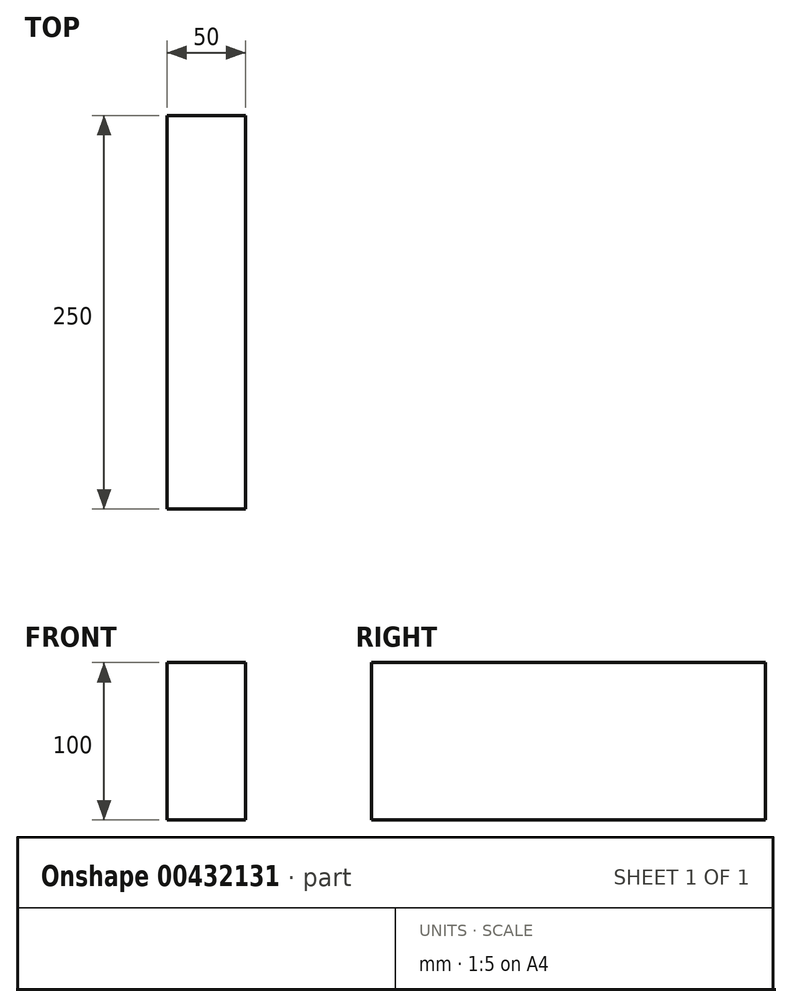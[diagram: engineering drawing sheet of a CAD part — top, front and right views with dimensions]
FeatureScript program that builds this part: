
annotation { "Feature Type Name" : "Feature", "Feature Type Description" : "" }
export const myFeature = defineFeature(function(context is Context, id is Id, definition is map)
    precondition{}
    {
        {
            var Q0;
            Q0=qCreatedBy(makeId("Right.planeOp"),FACE);
            var sketch = newSketch(context, id + "F0", { "sketchPlane" : qUnion([Q0])});
            skLineSegment(sketch, "E0.bottom", {"start": v(54.73, -201.24) * mm, "end": v(-195.27, -201.24) * mm});
            skLineSegment(sketch, "E0.top", {"start": v(54.73, -301.24) * mm, "end": v(-195.27, -301.24) * mm});
            skLineSegment(sketch, "E0.left", {"start": v(54.73, -201.24) * mm, "end": v(54.73, -301.24) * mm});
            skLineSegment(sketch, "E0.right", {"start": v(-195.27, -201.24) * mm, "end": v(-195.27, -301.24) * mm});
            skSolve(sketch);
        }
        {
            var Q0;
            Q0 = qSketchRegion(id + "F0", true);
            extrude(context, id + "F1", {"entities" : qUnion([Q0]), "depth" : 50 * mm});
        }
    });
